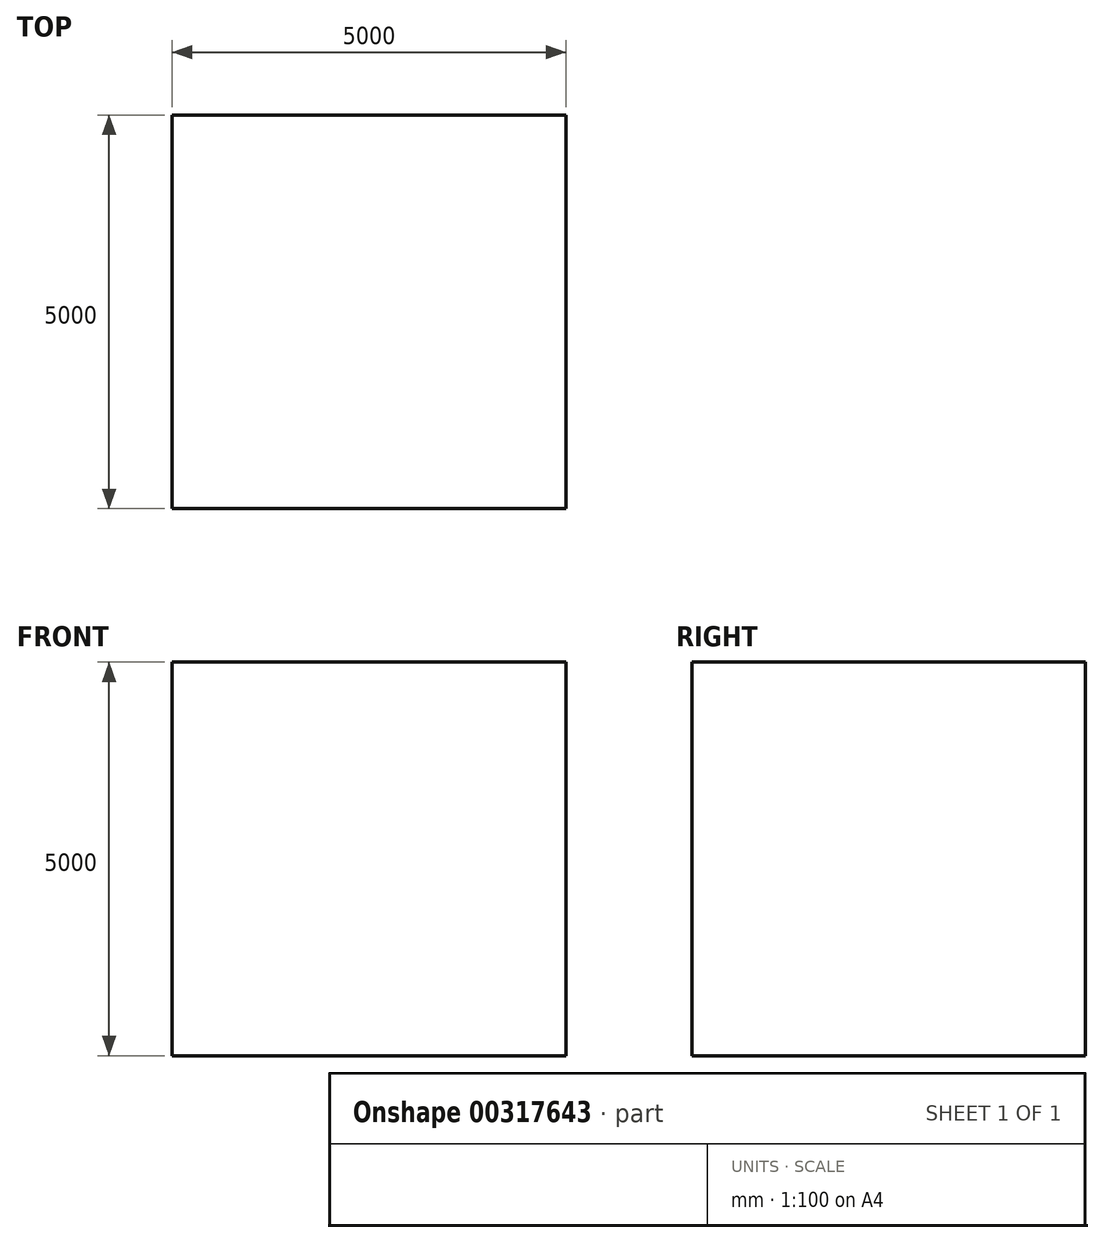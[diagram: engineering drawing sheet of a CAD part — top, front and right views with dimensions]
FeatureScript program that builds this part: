
annotation { "Feature Type Name" : "Feature", "Feature Type Description" : "" }
export const myFeature = defineFeature(function(context is Context, id is Id, definition is map)
    precondition{}
    {
        {
            var Q0;
            Q0=qCreatedBy(makeId("Front.planeOp"),FACE);
            var sketch = newSketch(context, id + "F0", { "sketchPlane" : qUnion([Q0])});
            skLineSegment(sketch, "E0", {"start": v(0, 5000) * mm, "end": v(0, 0) * mm});
            skLineSegment(sketch, "E1", {"start": v(0, 5000) * mm, "end": v(5000, 5000) * mm});
            skLineSegment(sketch, "E2", {"start": v(5000, 5000) * mm, "end": v(5000, 0) * mm});
            skLineSegment(sketch, "E3", {"start": v(5000, 0) * mm, "end": v(0, 0) * mm});
            skSolve(sketch);
        }
        {
            var Q0;
            Q0=makeQuery(id+"F0.imprint","IMPRINT",FACE,{"disambiguationData":[TD([[makeQuery(id+"F0.imprint","IMPRINT",EDGE,{"derivedFrom":sQuery(id+"F0.wireOp",EDGE,"E0")}),1.0]])]});
            extrude(context, id + "F1", {"entities" : qUnion([Q0]), "depth" : 5000 * mm});
        }
    });
